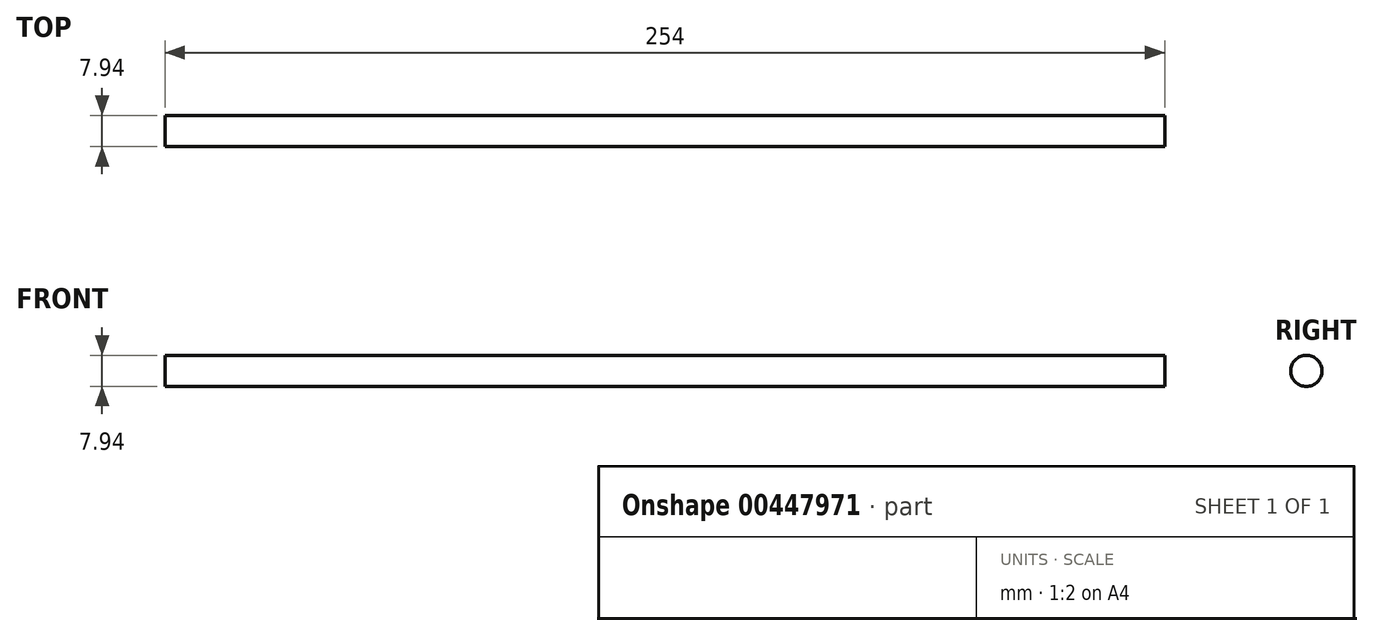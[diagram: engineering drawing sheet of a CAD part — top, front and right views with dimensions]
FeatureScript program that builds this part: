
annotation { "Feature Type Name" : "Feature", "Feature Type Description" : "" }
export const myFeature = defineFeature(function(context is Context, id is Id, definition is map)
    precondition{}
    {
        {
            var Q0;
            Q0=qCreatedBy(makeId("Right.planeOp"),FACE);
            var sketch = newSketch(context, id + "F0", { "sketchPlane" : qUnion([Q0])});
            skCircle(sketch, "E0", {"center": v(0, 0) * mm, "radius": 3.97 * mm});
            skSolve(sketch);
        }
        {
            var Q0;
            Q0=makeQuery(id+"F0.imprint","IMPRINT",FACE,{"disambiguationData":[TD([[makeQuery(id+"F0.imprint","IMPRINT",EDGE,{"derivedFrom":sQuery(id+"F0.wireOp",EDGE,"E0")}),1.0]])]});
            extrude(context, id + "F1", {"entities" : qUnion([Q0]), "depth" : 254 * mm});
        }
    });
